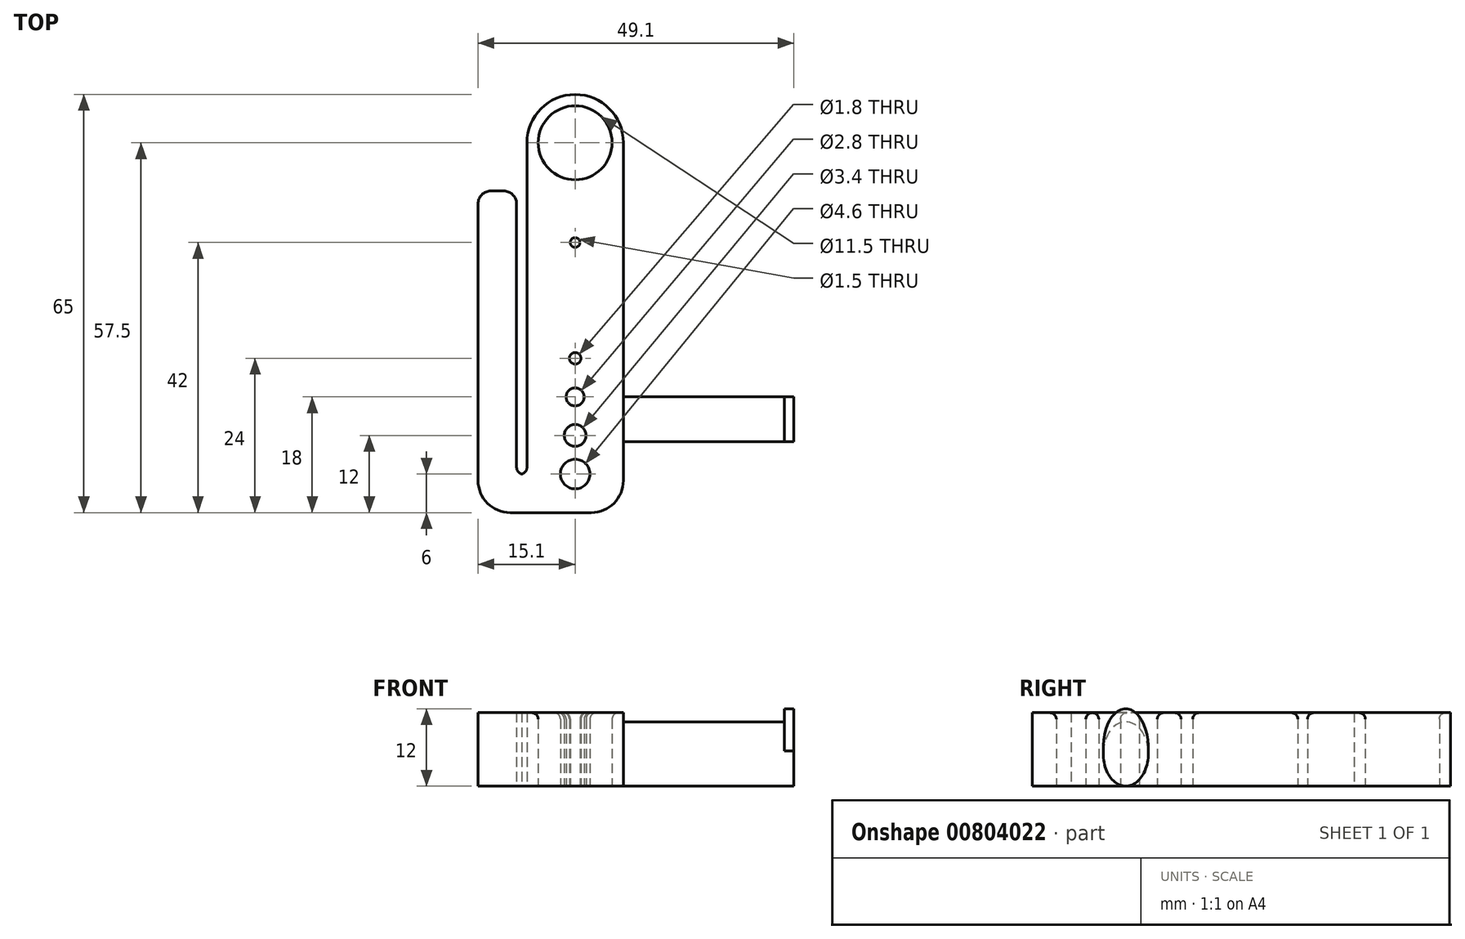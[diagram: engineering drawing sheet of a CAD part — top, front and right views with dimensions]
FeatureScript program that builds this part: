
annotation { "Feature Type Name" : "Feature", "Feature Type Description" : "" }
export const myFeature = defineFeature(function(context is Context, id is Id, definition is map)
    precondition{}
    {
        {
            var Q0;
            Q0=qCreatedBy(makeId("Top.planeOp"),FACE);
            var sketch = newSketch(context, id + "F0", { "sketchPlane" : qUnion([Q0])});
            skLineSegment(sketch, "E0.bottom", {"start": v(0, 0) * mm, "end": v(6, 0) * mm});
            skLineSegment(sketch, "E0.top", {"start": v(0, -50) * mm, "end": v(6, -50) * mm});
            skLineSegment(sketch, "E0.left", {"start": v(0, 0) * mm, "end": v(0, -50) * mm});
            skLineSegment(sketch, "E0.right", {"start": v(6, 0) * mm, "end": v(6, -50) * mm});
            skLineSegment(sketch, "E1", {"start": v(6, -50) * mm, "end": v(7.6, -50) * mm});
            skLineSegment(sketch, "E2", {"start": v(7.6, -50) * mm, "end": v(7.6, -44) * mm});
            skLineSegment(sketch, "E3", {"start": v(7.6, -44) * mm, "end": v(6, -44) * mm});
            skLineSegment(sketch, "E4.bottom", {"start": v(7.6, -50) * mm, "end": v(22.6, -50) * mm});
            skLineSegment(sketch, "E4.top", {"start": v(7.6, 15) * mm, "end": v(22.6, 15) * mm});
            skLineSegment(sketch, "E4.left", {"start": v(7.6, -50) * mm, "end": v(7.6, 15) * mm});
            skLineSegment(sketch, "E4.right", {"start": v(22.6, -50) * mm, "end": v(22.6, 15) * mm});
            skCircle(sketch, "E5", {"center": v(15.1, 7.5) * mm, "radius": 5.75 * mm});
            skLineSegment(sketch, "E6", {"start": v(15.1, -50) * mm, "end": v(15.1, -7.04) * mm, "construction": true});
            skCircle(sketch, "E7", {"center": v(15.1, -44) * mm, "radius": 2.3 * mm});
            skCircle(sketch, "E8", {"center": v(15.1, -38) * mm, "radius": 1.7 * mm});
            skCircle(sketch, "E9", {"center": v(15.1, -32) * mm, "radius": 1.4 * mm});
            skCircle(sketch, "E10", {"center": v(15.1, -26) * mm, "radius": 0.9 * mm});
            skCircle(sketch, "E11", {"center": v(15.1, -8) * mm, "radius": 0.75 * mm});
            skSolve(sketch);
        }
        {
            var Q0;
            Q0 = qSketchRegion(id + "F0", true);
            extrude(context, id + "F1", {"entities" : qUnion([Q0]), "depth" : 11.4 * mm, "offsetDistance" : 25 * mm});
        }
        {
            var Q0;
            Q0=makeQuery(id+"F1.opExtrude","SWEPT_EDGE",EDGE,{"disambiguationData":[OSD([sQuery(id+"F0.wireOp",EDGE,"E0.top"),sQuery(id+"F0.wireOp",EDGE,"E0.left")])]});
            var Q1;
            Q1=makeQuery(id+"F1.opExtrude","SWEPT_EDGE",EDGE,{"disambiguationData":[OSD([sQuery(id+"F0.wireOp",EDGE,"E4.bottom"),sQuery(id+"F0.wireOp",EDGE,"E4.right")])]});
            fillet(context, id + "F2", {"entities" : qUnion([Q0, Q1]), "radius" : 5 * mm, "tangentPropagation" : true, "allowEdgeOverflow" : false});
        }
        {
            var Q0;
            Q0=makeQuery(id+"F1.opExtrude","SWEPT_EDGE",EDGE,{"disambiguationData":[OSD([sQuery(id+"F0.wireOp",EDGE,"E4.top"),sQuery(id+"F0.wireOp",EDGE,"E4.right")])]});
            var Q1;
            Q1=makeQuery(id+"F1.opExtrude","SWEPT_EDGE",EDGE,{"disambiguationData":[OSD([sQuery(id+"F0.wireOp",EDGE,"E4.top"),sQuery(id+"F0.wireOp",EDGE,"E4.left")])]});
            fillet(context, id + "F3", {"entities" : qUnion([Q0, Q1]), "radius" : 7.5 * mm, "tangentPropagation" : true, "allowEdgeOverflow" : false});
        }
        {
            var Q0;
            Q0=makeQuery(id+"F1.opExtrude","SWEPT_EDGE",EDGE,{"disambiguationData":[OSD([sQuery(id+"F0.wireOp",EDGE,"E0.bottom"),sQuery(id+"F0.wireOp",EDGE,"E0.left")])]});
            var Q1;
            Q1=makeQuery(id+"F1.opExtrude","SWEPT_EDGE",EDGE,{"disambiguationData":[OSD([sQuery(id+"F0.wireOp",EDGE,"E0.bottom"),sQuery(id+"F0.wireOp",EDGE,"E0.right")])]});
            fillet(context, id + "F4", {"entities" : qUnion([Q0, Q1]), "radius" : 2 * mm, "tangentPropagation" : true, "allowEdgeOverflow" : false});
        }
        {
            var Q0;
            Q0=makeQuery(id+"F1.opExtrude","CAP_EDGE",EDGE,{"disambiguationData":[OSD([sQuery(id+"F0.wireOp",EDGE,"E7")])],"isStart":false});
            var Q1;
            Q1=makeQuery(id+"F1.opExtrude","CAP_EDGE",EDGE,{"disambiguationData":[OSD([sQuery(id+"F0.wireOp",EDGE,"E8")])],"isStart":false});
            var Q2;
            Q2=makeQuery(id+"F1.opExtrude","CAP_EDGE",EDGE,{"disambiguationData":[OSD([sQuery(id+"F0.wireOp",EDGE,"E9")])],"isStart":false});
            var Q3;
            Q3=makeQuery(id+"F1.opExtrude","CAP_EDGE",EDGE,{"disambiguationData":[OSD([sQuery(id+"F0.wireOp",EDGE,"E10")])],"isStart":false});
            var Q4;
            Q4=makeQuery(id+"F1.opExtrude","CAP_EDGE",EDGE,{"disambiguationData":[OSD([sQuery(id+"F0.wireOp",EDGE,"E11")])],"isStart":false});
            var Q5;
            Q5=makeQuery(id+"F1.opExtrude","SWEPT_EDGE",EDGE,{"disambiguationData":[OSD([sQuery(id+"F0.wireOp",EDGE,"E0.right"),sQuery(id+"F0.wireOp",EDGE,"E3")])]});
            var Q6;
            Q6=makeQuery(id+"F1.opExtrude","SWEPT_EDGE",EDGE,{"disambiguationData":[OSD([sQuery(id+"F0.wireOp",EDGE,"E3"),sQuery(id+"F0.wireOp",EDGE,"E4.left")])]});
            fillet(context, id + "F5", {"entities" : qUnion([Q0, Q1, Q2, Q3, Q4, Q5, Q6]), "radius" : 1 * mm, "tangentPropagation" : true, "allowEdgeOverflow" : false});
        }
        {
            var Q0;
            Q0=makeQuery(id+"F1.opExtrude","CAP_EDGE",EDGE,{"disambiguationData":[OSD([sQuery(id+"F0.wireOp",EDGE,"E5")])],"isStart":false});
            fillet(context, id + "F6", {"entities" : qUnion([Q0]), "radius" : 1 * mm, "tangentPropagation" : true, "allowEdgeOverflow" : false});
        }
        {
            var Q0;
            Q0=makeQuery(id+"F1.opExtrude","SWEPT_FACE",FACE,{"disambiguationData":[OSD([sQuery(id+"F0.wireOp",EDGE,"E4.right")])]});
            var sketch = newSketch(context, id + "F7", { "sketchPlane" : qUnion([Q0])});
            skEllipse(sketch, "E12", {"center": v(-35.5, 5) * mm, "majorRadius": 5 * mm, "minorRadius": 3.5 * mm, "majorAxis": v(0, -1)});
            skSolve(sketch);
        }
        {
            var Q0;
            Q0=makeQuery(id+"F7.imprint","IMPRINT",FACE,{"disambiguationData":[TD([[makeQuery(id+"F7.imprint","IMPRINT",EDGE,{"derivedFrom":sQuery(id+"F7.wireOp",EDGE,"E12")}),1.0]])]});
            extrude(context, id + "F8", {"entities" : qUnion([Q0]), "operationType" : NewBodyOperationType.ADD, "depth" : 25 * mm, "offsetDistance" : 25 * mm});
        }
        {
            var Q0;
            Q0=makeQuery(id+"F8.opExtrude","CAP_FACE",FACE,{"disambiguationData":[OSD([sQuery(id+"F7.wireOp",EDGE,"E12")])],"isStart":false});
            var sketch = newSketch(context, id + "F9", { "sketchPlane" : qUnion([Q0])});
            skEllipse(sketch, "E13", {"center": v(-35.5, 6) * mm, "majorRadius": 6 * mm, "minorRadius": 3.5 * mm, "majorAxis": v(0, -1)});
            skSolve(sketch);
        }
        {
            var Q0;
            {var subQ0=sQuery(id+"F9.wireOp",EDGE,"E13");var subQ1=makeQuery(id+"F8.opExtrude","CAP_EDGE",EDGE,{"disambiguationData":[OSD([sQuery(id+"F7.wireOp",EDGE,"E12")])],"isStart":false});var subQ2=makeQuery(id+"F9.imprint","INTERSECT",VERTEX,{"disambiguationData":[OD(0.0)],"derivedFrom":[subQ1,subQ0]});Q0=makeQuery(id+"F9.imprint","IMPRINT",FACE,{"disambiguationData":[TD([[makeQuery(id+"F9.imprint","IMPRINT",EDGE,{"disambiguationData":[TD([[subQ2,-1.0]])],"derivedFrom":subQ0}),1.0]])]});}
            var Q1;
            {var subQ0=sQuery(id+"F9.wireOp",EDGE,"E13");var subQ1=makeQuery(id+"F8.opExtrude","CAP_EDGE",EDGE,{"disambiguationData":[OSD([sQuery(id+"F7.wireOp",EDGE,"E12")])],"isStart":false});var subQ2=makeQuery(id+"F9.imprint","INTERSECT",VERTEX,{"disambiguationData":[OD(0.0)],"derivedFrom":[subQ1,subQ0]});Q1=makeQuery(id+"F9.imprint","IMPRINT",FACE,{"disambiguationData":[TD([[makeQuery(id+"F9.imprint","IMPRINT",EDGE,{"disambiguationData":[TD([[subQ2,1.0]])],"derivedFrom":subQ0}),1.0]])]});}
            var Q2;
            {var subQ0=sQuery(id+"F9.wireOp",EDGE,"E13");var subQ1=makeQuery(id+"F8.opExtrude","CAP_EDGE",EDGE,{"disambiguationData":[OSD([sQuery(id+"F7.wireOp",EDGE,"E12")])],"isStart":false});var subQ2=makeQuery(id+"F9.imprint","INTERSECT",VERTEX,{"disambiguationData":[OD(1.0)],"derivedFrom":[subQ1,subQ0]});Q2=makeQuery(id+"F9.imprint","IMPRINT",FACE,{"disambiguationData":[TD([[makeQuery(id+"F9.imprint","IMPRINT",EDGE,{"disambiguationData":[TD([[subQ2,1.0]])],"derivedFrom":subQ0}),-1.0]])]});}
            var Q3;
            {var subQ0=sQuery(id+"F9.wireOp",EDGE,"E13");var subQ1=makeQuery(id+"F8.opExtrude","CAP_EDGE",EDGE,{"disambiguationData":[OSD([sQuery(id+"F7.wireOp",EDGE,"E12")])],"isStart":false});var subQ2=makeQuery(id+"F9.imprint","INTERSECT",VERTEX,{"disambiguationData":[OD(0.0)],"derivedFrom":[subQ1,subQ0]});Q3=makeQuery(id+"F9.imprint","IMPRINT",FACE,{"disambiguationData":[TD([[makeQuery(id+"F9.imprint","IMPRINT",EDGE,{"disambiguationData":[TD([[subQ2,1.0]])],"derivedFrom":subQ0}),-1.0]])]});}
            extrude(context, id + "F10", {"entities" : qUnion([Q0, Q1, Q2, Q3]), "operationType" : NewBodyOperationType.ADD, "depth" : 1.5 * mm, "offsetDistance" : 25 * mm});
        }
    });
